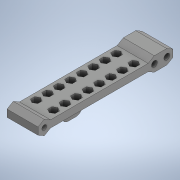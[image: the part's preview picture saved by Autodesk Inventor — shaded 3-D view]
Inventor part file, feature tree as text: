
AUTODESK INVENTOR PART (.ipt)
format: ipt  version: 2020 (Build 240168000, 168)  size: 554,496 bytes
history: native  units: in
note: dims shown in document units (in); Inventor stores cm internally (conversion verified against a paired STEP export)
features: sketch x7, extrude x6, projected_geometry x4, plane x2, mirror x1, fillet x1
ambient origin geometry x8: Origin, YZ Plane, XZ Plane, XY Plane, X Axis, Y Axis, Z Axis, Center Point
bodies: Solid1 (feature_tree)
feature tree (21):
  extrude  "Extrusion1"  Depth=3.4256in
  plane  "Work Plane1"
  extrude  "Extrusion2"  Depth=0.7874in
  sketch  "Sketch4"  dims[d4=0.0in d5=0.0906in]
  extrude  "Extrusion4"  Depth=0.0906in
  plane  "Work Plane2"
  extrude  "Extrusion6"  Depth=3.1106in
  mirror  "Mirror2"
  extrude  "Extrusion7"  Depth=0.315in
  extrude  "Extrusion8"  Depth=0.2362in
  fillet  "Fillet1"  [1 undecoded]
  sketch  "Sketch1"  dims[d0=0.1818in d1=3.4256in]
  sketch  "Sketch2"  dims[d2=0.122in d3=0.7874in]
  sketch  "Sketch5"  dims[d6=0.7874in d7=0.0in d28=3.1106in]
  sketch  "Sketch7"  dims[d29=0.315in d31=0.315in]
  projected_geometry  "Projected Loop7"
  projected_geometry  "Projected Loop8"
  sketch  "Sketch8"  dims[d33=0.1476in d34=0.2362in d35=0.0in]
  projected_geometry  "Projected Loop9"
  sketch  "Sketch10"  dims[d38=0.315in d39=0.2756in d40=-0.3092in d41=0.0787in d42=0.0787in d43=0.0787in d44=3.1496in d46=0.2913in d47=0.3937in d49=0.3937in d51=3.1496in d53=0.2913in d54=0.3937in d56=0.3937in d58=0.0in d59=0.0in d60=1.0994in d61=0.1378in d63=1.1811in d64=0.1575in d65=0.0in d66=0.126in d67=0.1575in]
  projected_geometry  "Projected Loop10"
note: 1 required parameter value undecoded (feature->parameter linkage not recoverable at this tier; creation-order binding heuristic only, values carry confidence <= 0.55)
